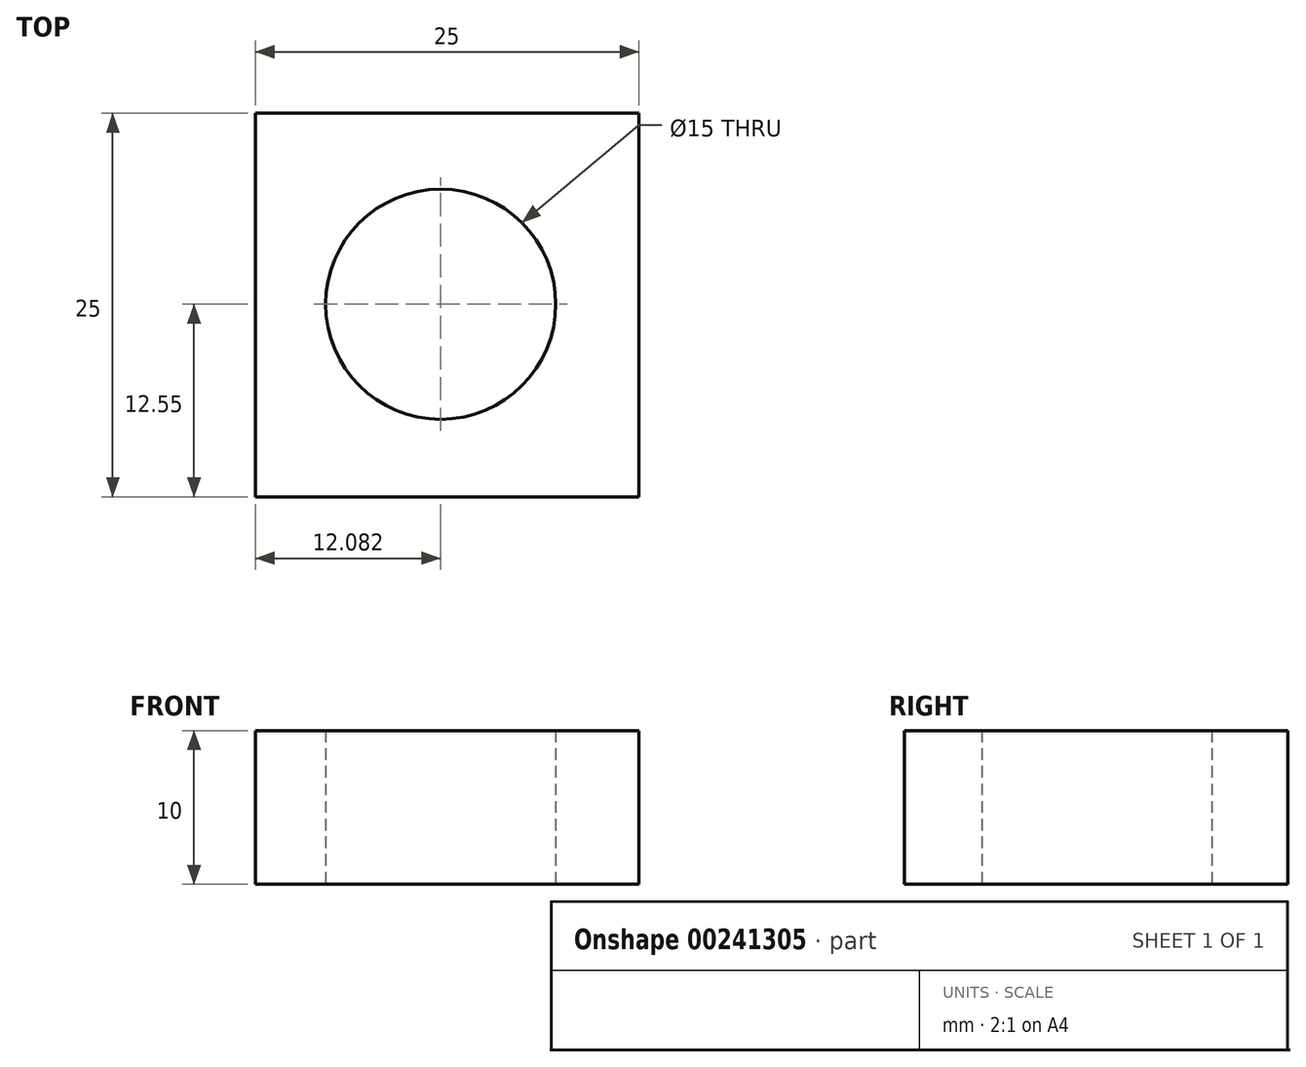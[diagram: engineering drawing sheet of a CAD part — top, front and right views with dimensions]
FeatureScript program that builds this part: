
annotation { "Feature Type Name" : "Feature", "Feature Type Description" : "" }
export const myFeature = defineFeature(function(context is Context, id is Id, definition is map)
    precondition{}
    {
        {
            var Q0;
            Q0=qCreatedBy(makeId("Top.planeOp"),FACE);
            var sketch = newSketch(context, id + "F0", { "sketchPlane" : qUnion([Q0])});
            skLineSegment(sketch, "E0.bottom", {"start": v(-94.74, 12.45) * mm, "end": v(-69.74, 12.45) * mm});
            skLineSegment(sketch, "E0.top", {"start": v(-94.74, -12.55) * mm, "end": v(-69.74, -12.55) * mm});
            skLineSegment(sketch, "E0.left", {"start": v(-94.74, 12.45) * mm, "end": v(-94.74, -12.55) * mm});
            skLineSegment(sketch, "E0.right", {"start": v(-69.74, 12.45) * mm, "end": v(-69.74, -12.55) * mm});
            skLineSegment(sketch, "E1", {"start": v(-69.74, -0.05) * mm, "end": v(-76.66, -0.05) * mm});
            skLineSegment(sketch, "E2", {"start": v(-82.24, -12.55) * mm, "end": v(-82.24, -4.64) * mm});
            skCircle(sketch, "E3", {"center": v(-82.66, 0) * mm, "radius": 7.5 * mm});
            skSolve(sketch);
        }
        {
            var Q0;
            Q0 = qSketchRegion(id + "F0", true);
            extrude(context, id + "F1", {"entities" : qUnion([Q0]), "depth" : 10 * mm});
        }
    });
